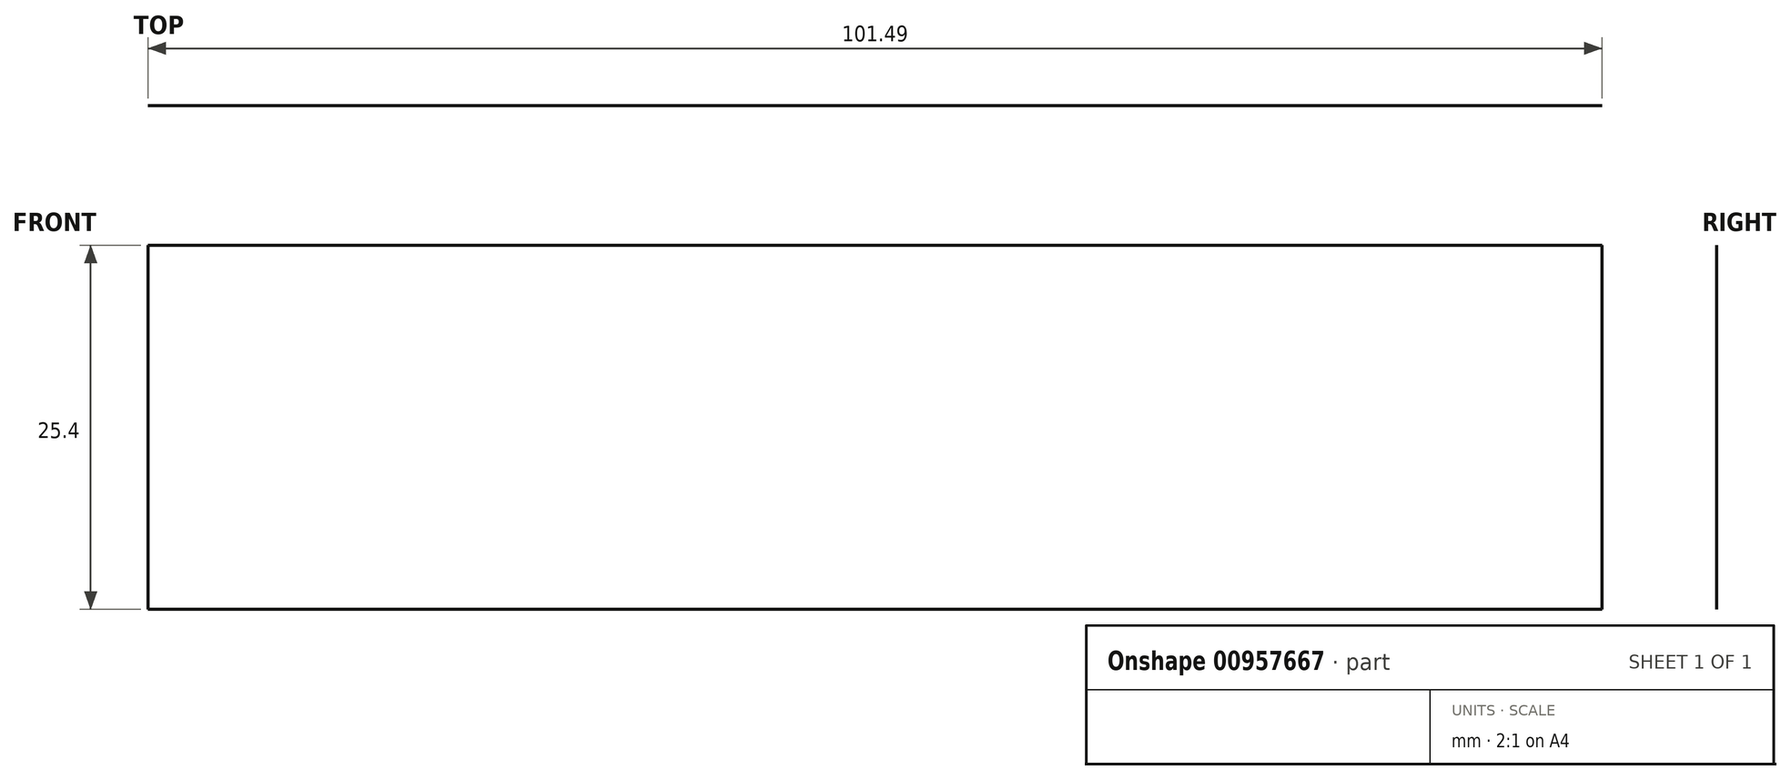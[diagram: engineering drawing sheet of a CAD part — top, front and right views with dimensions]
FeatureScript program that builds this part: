
annotation { "Feature Type Name" : "Feature", "Feature Type Description" : "" }
export const myFeature = defineFeature(function(context is Context, id is Id, definition is map)
    precondition{}
    {
        {
            var Q0;
            Q0=qCreatedBy(makeId("Top.planeOp"),FACE);
            var sketch = newSketch(context, id + "F0", { "sketchPlane" : qUnion([Q0])});
            skLineSegment(sketch, "E0.bottom", {"start": v(-49.7, 19.04) * mm, "end": v(51.8, 19.04) * mm});
            skLineSegment(sketch, "E0.top", {"start": v(-49.7, -11.15) * mm, "end": v(51.8, -11.15) * mm});
            skLineSegment(sketch, "E0.left", {"start": v(-49.7, 19.04) * mm, "end": v(-49.7, -11.15) * mm});
            skLineSegment(sketch, "E0.right", {"start": v(51.8, 19.04) * mm, "end": v(51.8, -11.15) * mm});
            skSolve(sketch);
        }
        {
            var Q0;
            Q0=sQuery(id+"F0.wireOp",EDGE,"E0.bottom");
            extrude(context, id + "F1", {"bodyType" : ToolBodyType.SURFACE, "surfaceEntities" : qUnion([Q0]), "depth" : 25.4 * mm, "offsetDistance" : 25.4 * mm});
        }
    });
